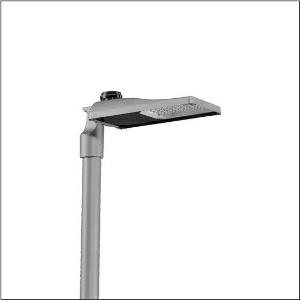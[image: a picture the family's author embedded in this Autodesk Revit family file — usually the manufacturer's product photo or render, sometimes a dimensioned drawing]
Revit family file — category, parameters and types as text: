
# Revit family: streetlight_sl_31_mini___st1_0a_5xh2d3bn08ga_9766
name_source: partatom
category: Lighting Fixtures
units: mm (PartAtom-declared; Revit-internal decimal feet)

## family parameters
Cut with Voids When Loaded = No
Host = Face
Light Source = No
Part Type = Normal
Room Calculation Point = No
Round Connector Dimension = Use Diameter
Shared = No

## types (1)
- --- (1 x LED, 5710 lm, 37.3 W, 3000K)
    Apparent Load = 37 VA
    CIE Flux Codes = 37 72 97 100 100
    Color Rendering = 70
    Color Temperature = 3000K
    Default Elevation = 1800 mm
    Description = Streetlight SL 31 mini NEMA (7pin) mast luminaire for post-top, side-entry; light control with lens of PMMA; light distribution: ST1.0a, direct asymmetric distribution, for standard-compliant lighting for roads and squares; LED: luminous flux: 5.710lm, light colour: 730, colour temperature: 3000K; luminous efficacy: 153,1lm/W; control: overheat protection, intelligent temperature release in ECG and LED module, constant luminous flux control, time-dependent luminous flux control, flexible luminous flux parameterisation, pre-setting: linear dimming characteristic; luminaire housing, of diecast aluminium, SITECO metallic grey (DB 702S), corrosivity category C5 high according to DIN EN ISO 12944; cover of toughened safety glass, transparent, mast flange of diecast aluminium, SITECO metallic grey (DB 702S), spigot size: 76/60mm, mast flange included unmounted; cable length: 6,5m, connection cable pre-assembled; mains connection: 220..240V, AC, 50/60Hz; power consumption (at start of service life): 37,3W / (at end of service life): 38,7W / (with reduced operation 50%): 17,5W; protection rating (complete): IP66; insulation class (complete): insulation class I (protective earthing); impact resistance: IK10; certification: CE, ENEC, ENEC+, VDE, UKCA; permissible operating ambient temperature for outdoor applications: -40..+50°C; packaging unit: 1 piece

Light Distribution: ST1.0a
    Height = 76 mm
    Lamp = 1 x LED
    Lamp Light Flux = 5710 lm
    Lamp Power = 37.3 W
    Lamp count = 1
    Length = 547 mm
    Luminous efficacy = 153 lm/W
    Manufacturer = Siteco
    ModVariant = No
    Model = 5XH2D3BN08GA
    Number of Poles = 1
    OnlyDefault = Yes
    Power Factor = 1
    Product Name = Streetlight SL 31 mini | ST1.0a
    Product group = mast luminaire | pylon top
    ProductGroupID = 6100
    Protection Class = Protection class I
    Protection Degree = IP 66
    RLX_Detail_Level = 1
    RLX_Emergency_Light_Flux = 0 lm
    RLX_Emergency_Type = 0
    RLX_Emergency_Type_DB = No
    RlxData = <blob elided: 40065 chars, md5=de947c46>
    Socket = socket
    Standby Power = 0 W
    System Light Flux = 5710 lm
    System Power = 37 W
    Type Comments = factory setting: luminous flux: 100 % | dim-lin: 254 | 386 mA
    Type Image = l_1300322.jpg
    URL = http://relux.com
    VarID = @adj_061293
    Voltage = 0 V
    Weight = 0.00 kg
    Width = 265 mm

## geometry (parser evidence)
native form markers: Blend x4, Sweep x10
no freeform markers — native parametric forms only
